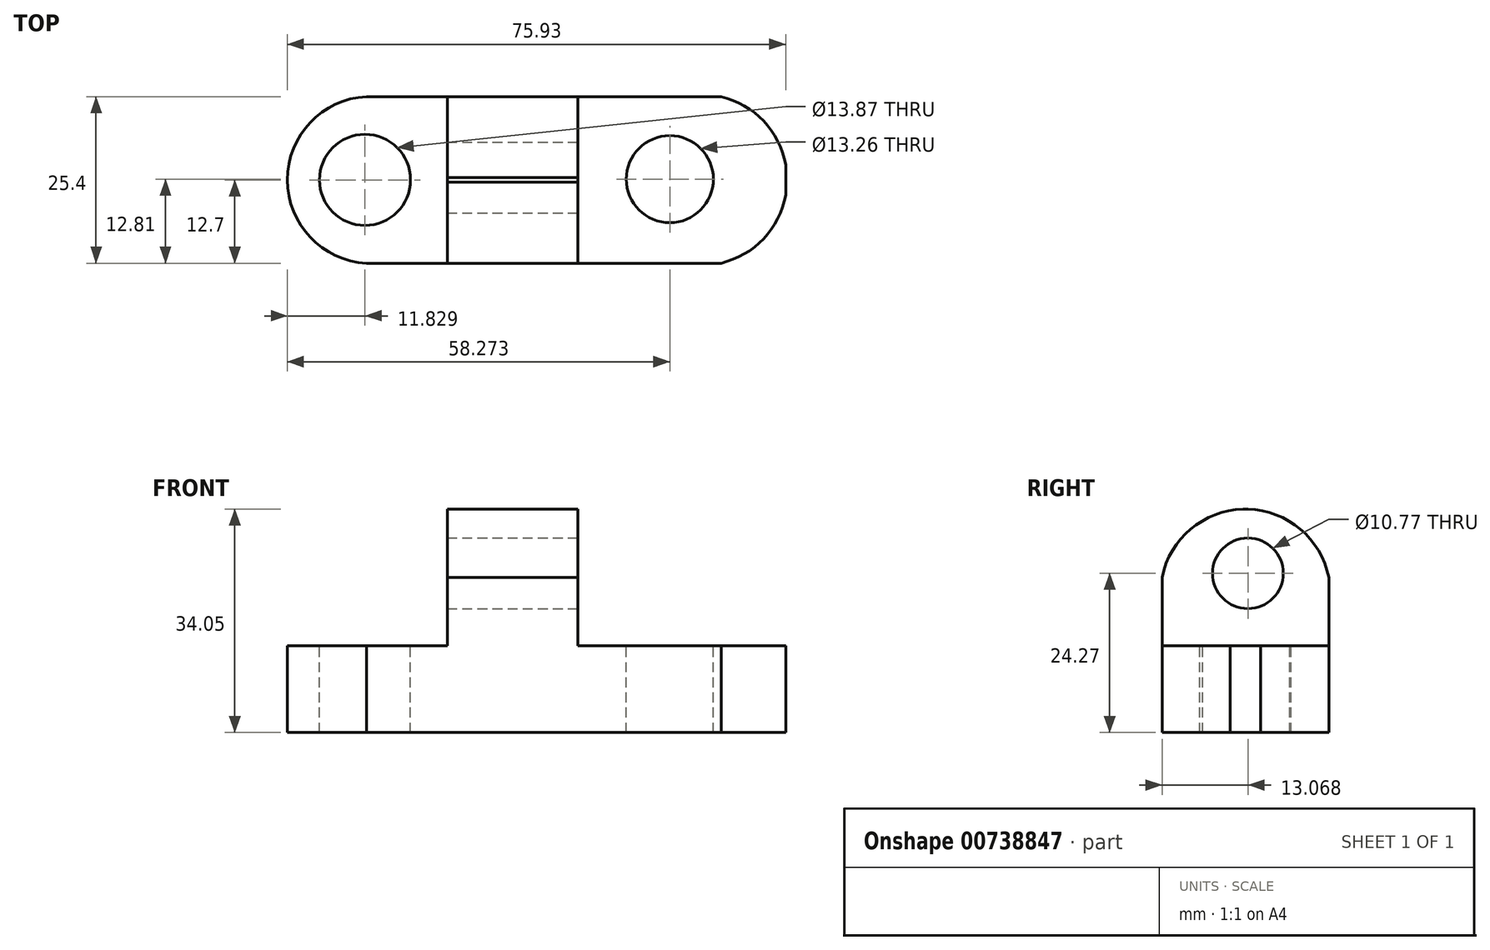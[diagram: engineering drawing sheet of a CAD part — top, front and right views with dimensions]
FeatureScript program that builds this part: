
annotation { "Feature Type Name" : "Feature", "Feature Type Description" : "" }
export const myFeature = defineFeature(function(context is Context, id is Id, definition is map)
    precondition{}
    {
        {
            var Q0;
            Q0=qCreatedBy(makeId("Front.planeOp"),FACE);
            var sketch = newSketch(context, id + "F0", { "sketchPlane" : qUnion([Q0])});
            skLineSegment(sketch, "E0", {"start": v(0, 0) * mm, "end": v(76.19, 0) * mm});
            skLineSegment(sketch, "E1", {"start": v(76.19, 0) * mm, "end": v(76.19, 13.25) * mm});
            skLineSegment(sketch, "E2", {"start": v(76.19, 13.25) * mm, "end": v(44.54, 13.25) * mm});
            skLineSegment(sketch, "E3", {"start": v(44.54, 13.25) * mm, "end": v(44.54, 34.05) * mm});
            skLineSegment(sketch, "E4", {"start": v(44.54, 34.05) * mm, "end": v(24.63, 34.05) * mm});
            skLineSegment(sketch, "E5", {"start": v(24.63, 34.05) * mm, "end": v(24.63, 13.25) * mm});
            skLineSegment(sketch, "E6", {"start": v(24.63, 13.25) * mm, "end": v(0, 13.25) * mm});
            skLineSegment(sketch, "E7", {"start": v(0, 13.25) * mm, "end": v(0, 0) * mm});
            skSolve(sketch);
        }
        {
            var Q0;
            Q0 = qSketchRegion(id + "F0", true);
            extrude(context, id + "F1", {"entities" : qUnion([Q0]), "depth" : 25.4 * mm, "offsetDistance" : 25.4 * mm});
        }
        {
            var Q0;
            Q0=makeQuery(id+"F1.opExtrude","SWEPT_FACE",FACE,{"disambiguationData":[OSD([sQuery(id+"F0.wireOp",EDGE,"E2")])]});
            var sketch = newSketch(context, id + "F2", { "sketchPlane" : qUnion([Q0])});
            skCircle(sketch, "E8", {"center": v(58.53, -12.6) * mm, "radius": 6.63 * mm});
            skCircle(sketch, "E9", {"center": v(12.09, -12.7) * mm, "radius": 6.94 * mm});
            skPoint(sketch, "E9.centerSnap0", {"position": v(44.54, -12.7) * mm});
            skSolve(sketch);
        }
        {
            var Q0;
            Q0=makeQuery(id+"F2.imprint","IMPRINT",FACE,{"disambiguationData":[TD([[makeQuery(id+"F2.imprint","IMPRINT",EDGE,{"derivedFrom":sQuery(id+"F2.wireOp",EDGE,"E9")}),1.0]])]});
            var Q1;
            Q1=makeQuery(id+"F2.imprint","IMPRINT",FACE,{"disambiguationData":[TD([[makeQuery(id+"F2.imprint","IMPRINT",EDGE,{"derivedFrom":sQuery(id+"F2.wireOp",EDGE,"E8")}),1.0]])]});
            extrude(context, id + "F3", {"entities" : qUnion([Q0, Q1]), "operationType" : NewBodyOperationType.REMOVE, "endBound" : BoundingType.THROUGH_ALL, "oppositeDirection" : true, "depth" : 25.4 * mm, "offsetDistance" : 25.4 * mm});
        }
        {
            var Q0;
            Q0=makeQuery(id+"F1.opExtrude","SWEPT_FACE",FACE,{"disambiguationData":[OSD([sQuery(id+"F0.wireOp",EDGE,"E3")])]});
            var sketch = newSketch(context, id + "F4", { "sketchPlane" : qUnion([Q0])});
            skArc(sketch, "E10", {"start": v(0, 23.65) * mm, "mid": v(-12.7, 34.05) * mm, "end": v(-25.4, 23.65) * mm});
            skSolve(sketch);
        }
        {
            var Q0;
            {var subQ0=sQuery(id+"F4.wireOp",EDGE,"E10");var subQ1=sQuery(id+"F0.wireOp",EDGE,"E3");var subQ2=makeQuery(id+"F1.opExtrude","CAP_EDGE",EDGE,{"disambiguationData":[OSD([subQ1])],"isStart":false});var subQ3=makeQuery(id+"F4.imprint","INTERSECT",VERTEX,{"derivedFrom":[subQ2,subQ0]});Q0=makeQuery(id+"F4.imprint","IMPRINT",FACE,{"disambiguationData":[TD([[makeQuery(id+"F4.imprint","IMPRINT",EDGE,{"disambiguationData":[TD([[subQ3,1.0]])],"derivedFrom":subQ0}),-1.0]])]});}
            var Q1;
            {var subQ0=sQuery(id+"F4.wireOp",EDGE,"E10");var subQ1=sQuery(id+"F0.wireOp",EDGE,"E3");var subQ2=makeQuery(id+"F1.opExtrude","CAP_EDGE",EDGE,{"disambiguationData":[OSD([subQ1])],"isStart":true});var subQ3=makeQuery(id+"F4.imprint","INTERSECT",VERTEX,{"derivedFrom":[subQ2,subQ0]});Q1=makeQuery(id+"F4.imprint","IMPRINT",FACE,{"disambiguationData":[TD([[makeQuery(id+"F4.imprint","IMPRINT",EDGE,{"disambiguationData":[TD([[subQ3,-1.0]])],"derivedFrom":subQ0}),-1.0]])]});}
            extrude(context, id + "F5", {"entities" : qUnion([Q0, Q1]), "operationType" : NewBodyOperationType.REMOVE, "endBound" : BoundingType.THROUGH_ALL, "oppositeDirection" : true, "depth" : 25.4 * mm, "offsetDistance" : 25.4 * mm});
        }
        {
            var Q0;
            Q0=makeQuery(id+"F1.opExtrude","SWEPT_FACE",FACE,{"disambiguationData":[OSD([sQuery(id+"F0.wireOp",EDGE,"E3")])]});
            var sketch = newSketch(context, id + "F6", { "sketchPlane" : qUnion([Q0])});
            skCircle(sketch, "E11", {"center": v(-12.33, 24.27) * mm, "radius": 5.39 * mm});
            skSolve(sketch);
        }
        {
            var Q0;
            Q0=makeQuery(id+"F6.imprint","IMPRINT",FACE,{"disambiguationData":[TD([[makeQuery(id+"F6.imprint","IMPRINT",EDGE,{"derivedFrom":sQuery(id+"F6.wireOp",EDGE,"E11")}),1.0]])]});
            extrude(context, id + "F7", {"entities" : qUnion([Q0]), "operationType" : NewBodyOperationType.REMOVE, "endBound" : BoundingType.THROUGH_ALL, "oppositeDirection" : true, "depth" : 25.4 * mm, "offsetDistance" : 25.4 * mm});
        }
        {
            var Q0;
            Q0=makeQuery(id+"F1.opExtrude","SWEPT_FACE",FACE,{"disambiguationData":[OSD([sQuery(id+"F0.wireOp",EDGE,"E6")])]});
            var sketch = newSketch(context, id + "F8", { "sketchPlane" : qUnion([Q0])});
            skArc(sketch, "E12", {"start": v(12.31, 0) * mm, "mid": v(0.26, -12.7) * mm, "end": v(12.31, -25.4) * mm});
            skArc(sketch, "E13", {"start": v(59.3, -25.51) * mm, "mid": v(76.19, -12.52) * mm, "end": v(58.94, 0) * mm});
            skSolve(sketch);
        }
        {
            var Q0;
            {var subQ0=sQuery(id+"F8.wireOp",EDGE,"E12");Q0=makeQuery(id+"F8.imprint","IMPRINT",FACE,{"disambiguationData":[TD([[makeQuery(id+"F8.imprint","IMPRINT",EDGE,{"derivedFrom":subQ0}),-1.0]])]});}
            extrude(context, id + "F9", {"entities" : qUnion([Q0]), "operationType" : NewBodyOperationType.REMOVE, "endBound" : BoundingType.THROUGH_ALL, "oppositeDirection" : true, "depth" : 25.4 * mm, "offsetDistance" : 25.4 * mm});
        }
        {
            var Q0;
            Q0=makeQuery(id+"F1.opExtrude","SWEPT_FACE",FACE,{"disambiguationData":[OSD([sQuery(id+"F0.wireOp",EDGE,"E2")])]});
            var sketch = newSketch(context, id + "F10", { "sketchPlane" : qUnion([Q0])});
            skArc(sketch, "E14", {"start": v(60.36, -25.4) * mm, "mid": v(76.4, -12.7) * mm, "end": v(60.36, 0) * mm});
            skSolve(sketch);
        }
        {
            var Q0;
            {var subQ0=sQuery(id+"F10.wireOp",EDGE,"E14");var subQ1=sQuery(id+"F0.wireOp",EDGE,"E2");var subQ4=makeQuery(id+"F1.opExtrude","CAP_EDGE",EDGE,{"disambiguationData":[OSD([subQ1])],"isStart":true});var subQ5=makeQuery(id+"F10.imprint","INTERSECT",VERTEX,{"disambiguationData":[OD(1.0)],"derivedFrom":[subQ4,subQ0]});Q0=makeQuery(id+"F10.imprint","IMPRINT",FACE,{"disambiguationData":[TD([[makeQuery(id+"F10.imprint","IMPRINT",EDGE,{"disambiguationData":[TD([[subQ5,1.0]])],"derivedFrom":subQ0}),-1.0]])]});}
            var Q1;
            {var subQ0=sQuery(id+"F10.wireOp",EDGE,"E14");var subQ1=sQuery(id+"F0.wireOp",EDGE,"E2");var subQ2=makeQuery(id+"F1.opExtrude","CAP_EDGE",EDGE,{"disambiguationData":[OSD([subQ1])],"isStart":false});var subQ3=makeQuery(id+"F10.imprint","INTERSECT",VERTEX,{"disambiguationData":[OD(1.0)],"derivedFrom":[subQ2,subQ0]});Q1=makeQuery(id+"F10.imprint","IMPRINT",FACE,{"disambiguationData":[TD([[makeQuery(id+"F10.imprint","IMPRINT",EDGE,{"disambiguationData":[TD([[subQ3,-1.0]])],"derivedFrom":subQ0}),-1.0]])]});}
            extrude(context, id + "F11", {"entities" : qUnion([Q0, Q1]), "operationType" : NewBodyOperationType.REMOVE, "endBound" : BoundingType.THROUGH_ALL, "oppositeDirection" : true, "depth" : 25.4 * mm, "offsetDistance" : 25.4 * mm});
        }
    });
